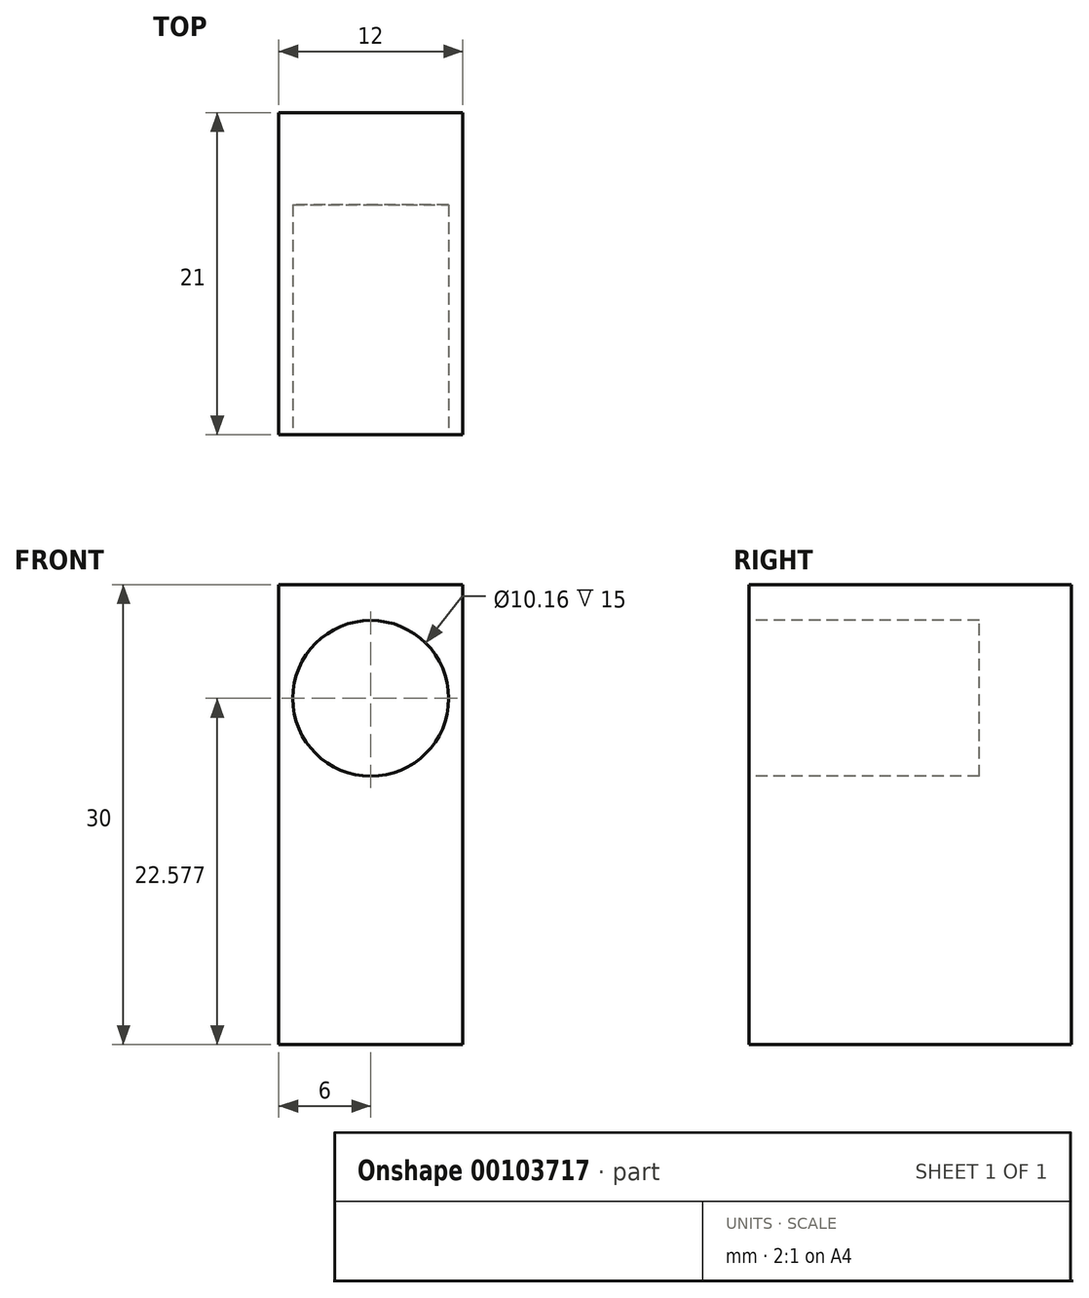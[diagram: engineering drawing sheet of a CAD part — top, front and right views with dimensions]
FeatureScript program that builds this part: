
annotation { "Feature Type Name" : "Feature", "Feature Type Description" : "" }
export const myFeature = defineFeature(function(context is Context, id is Id, definition is map)
    precondition{}
    {
        {
            var Q0;
            Q0=qCreatedBy(makeId("Front.planeOp"),FACE);
            var sketch = newSketch(context, id + "F0", { "sketchPlane" : qUnion([Q0])});
            skLineSegment(sketch, "E0.bottom", {"start": v(-6, 15) * mm, "end": v(6, 15) * mm});
            skLineSegment(sketch, "E0.top", {"start": v(-6, -15) * mm, "end": v(6, -15) * mm});
            skLineSegment(sketch, "E0.left", {"start": v(-6, 15) * mm, "end": v(-6, -15) * mm});
            skLineSegment(sketch, "E0.right", {"start": v(6, 15) * mm, "end": v(6, -15) * mm});
            skPoint(sketch, "E0.middle", {"position": v(0, 0) * mm});
            skSolve(sketch);
        }
        {
            var Q0;
            Q0=makeQuery(id+"F0.imprint","IMPRINT",FACE,{"disambiguationData":[TD([[makeQuery(id+"F0.imprint","IMPRINT",EDGE,{"derivedFrom":sQuery(id+"F0.wireOp",EDGE,"E0.bottom")}),-1.0]])]});
            extrude(context, id + "F1", {"entities" : qUnion([Q0]), "depth" : 21 * mm});
        }
        {
            var Q0;
            Q0=makeQuery(id+"F1.opExtrude","CAP_FACE",FACE,{"disambiguationData":[OSD([sQuery(id+"F0.wireOp",EDGE,"E0.bottom"),sQuery(id+"F0.wireOp",EDGE,"E0.top"),sQuery(id+"F0.wireOp",EDGE,"E0.left"),sQuery(id+"F0.wireOp",EDGE,"E0.right")])],"isStart":false});
            var sketch = newSketch(context, id + "F2", { "sketchPlane" : qUnion([Q0])});
            skCircle(sketch, "E1", {"center": v(0, 7.58) * mm, "radius": 5.08 * mm});
            skSolve(sketch);
        }
        {
            var Q0;
            Q0=makeQuery(id+"F2.imprint","IMPRINT",FACE,{"disambiguationData":[TD([[makeQuery(id+"F2.imprint","IMPRINT",EDGE,{"derivedFrom":sQuery(id+"F2.wireOp",EDGE,"E1")}),1.0]])]});
            var Q1;
            Q1=sQuery(id+"F2.wireOp",EDGE,"E1");
            extrude(context, id + "F3", {"entities" : qUnion([Q0]), "operationType" : NewBodyOperationType.REMOVE, "surfaceEntities" : qUnion([Q1]), "oppositeDirection" : true, "depth" : 15 * mm});
        }
    });
